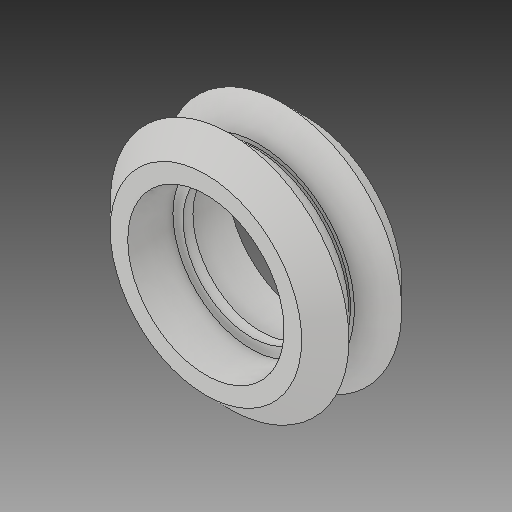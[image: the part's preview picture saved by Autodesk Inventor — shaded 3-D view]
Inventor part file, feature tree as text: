
AUTODESK INVENTOR PART (.ipt)
format: ipt  version: 2018 (Build 220112000, 112)  size: 160,256 bytes
history: native  units: mm
features: sketch x5, other x3
ambient origin geometry x8: Origin, YZ Plane, XZ Plane, XY Plane, X Axis, Y Axis, Z Axis, Center Point
bodies: Solid1 (feature_tree)
feature tree (8):
  other  "dELRIN.ipt"
  other  "Solid1::dELRIN.ipt"
  other  "TaggingFeature1"
  sketch  "Sketch1"  dims[d0=10.0mm]
  sketch  "Sketch2"
  sketch  "Sketch3"
  sketch  "Sketch4"
  sketch  "Sketch5"
